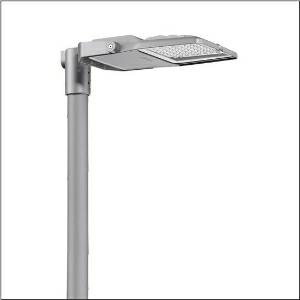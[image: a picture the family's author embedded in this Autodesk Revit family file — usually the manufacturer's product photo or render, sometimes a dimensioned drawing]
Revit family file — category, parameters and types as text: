
# Revit family: floodlight_fl_21_iq_mini___pl64_5xa7771b4e3a_3408
name_source: partatom
category: Lighting Fixtures
units: mm (PartAtom-declared; Revit-internal decimal feet)

## family parameters
Cut with Voids When Loaded = No
Host = Face
Light Source = No
Part Type = Normal
Room Calculation Point = No
Round Connector Dimension = Use Diameter
Shared = No

## types (1)
- --- (1 x LED, 6270 lm, 45.5 W, 4000K)
    Apparent Load = 46 VA
    CIE Flux Codes = 28 80 98 100 100
    Color Rendering = 70
    Color Temperature = 4000K
    Default Elevation = 1800 mm
    Description = Floodlight FL 21 iQ mini, floodlight, primary light control with lens, of PMMA, primary optical cover: protective disc, of toughened safety glass, transparent, light distribution: PL64, light emission: direct distribution, installation type: surface-mounted, lamps: LED, High Power LED, rated values: 6.270lm | 45,5W | 137,8lm/W (begin service life); end service life: 6.270lm | 48W; at 50% lumin. flux: 3.135lm | 21,5W | 145,8lm/W, colour temperature: 4000K, colour rendering: CRI > 70, light colour: 740, light setting 1 begin service life: 100% | 6.270lm | 45,5W | 137,8lm/W | 4.000K, light setting 1 end service life: 48W, further light settings possible, control: Auto-Match, Temp-Guard, Lumen-Switch, Night-Set, Smart-Wire, Light-Fading, Desk-Remote (wireless, voltage-free reading and setting of iQ features in the workshop via application-optimized NFC function/RFID function), optimised constant luminous flux control (CLO 2.0), pre-setting: linear dimming characteristic, with terminal, 6-pole, mains connection: 220..240V, AC, 50/60Hz, luminaire housing, of diecast aluminium, powder-coated, SITECO metallic grey (DB 702S), corrosivity category C5 mid according to DIN EN ISO 12944suitable for swimming poolschlorine-resistant, sealing non-destructively replaceable, please order mast flange separately, mast bracket, of steel, galvanised, powder-coated, SITECO metallic grey (DB 702S), protection rating (complete): IP66, insulation class (complete): insulation class II (safety insulation), certification: CE, ENEC, VDE, protection symbol: D, impact resistance: IK08, permissible operating ambient temperature: -40..+40°C, permissible operating ambient temperature for outdoor applications: -40..+50°C, standard: DIN EN 12944, LABS conformity tested according to VDMA 24364:2018-05, packaging unit: 1 piece

Light Distribution: PL64
    Height = 70 mm
    Lamp = 1 x LED
    Lamp Light Flux = 6270 lm
    Lamp Power = 45.5 W
    Lamp count = 1
    Length = 485 mm
    Luminous efficacy = 138 lm/W
    Manufacturer = Siteco
    ModVariant = No
    Model = 5XA7771B4E3A
    Number of Poles = 1
    OnlyDefault = Yes
    Power Factor = 1
    Product Name = Floodlight FL 21 iQ mini | PL64
    Product group = floodlight | pylon annexe
    ProductGroupID = 6201
    Protection Class = Protection class II
    Protection Degree = IP 66
    RLX_Detail_Level = 1
    RLX_Emergency_Light_Flux = 0 lm
    RLX_Emergency_Type = 0
    RLX_Emergency_Type_DB = No
    RlxData = <blob elided: 101625 chars, md5=9e1f6de6>
    Socket = socket
    Standby Power = 0 W
    System Light Flux = 6270 lm
    System Power = 46 W
    Type Comments = factory setting: luminous flux: 100 % | dim-lin: 254 | 463 mA
    Type Image = l_1007125.jpg
    URL = http://relux.com
    VarID = @adj_166523
    Voltage = 0 V
    Weight = 0.00 kg
    Width = 337 mm

## geometry (parser evidence)
native form markers: Blend x4, Sweep x12
no freeform markers — native parametric forms only
